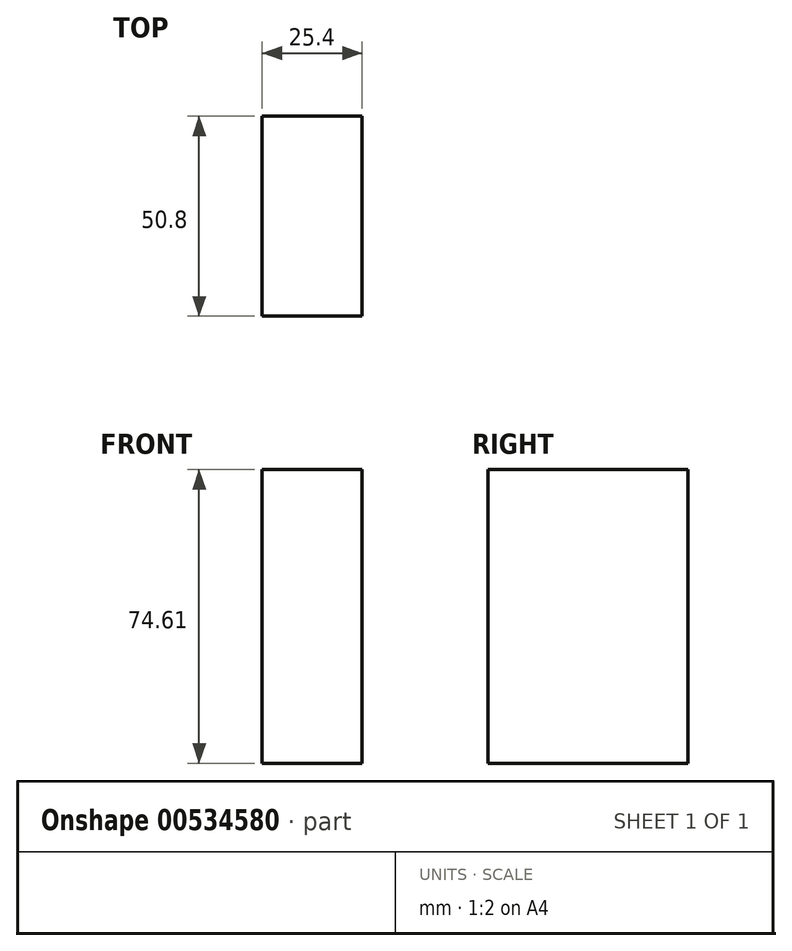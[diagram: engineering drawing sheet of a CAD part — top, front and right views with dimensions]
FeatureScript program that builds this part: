
annotation { "Feature Type Name" : "Feature", "Feature Type Description" : "" }
export const myFeature = defineFeature(function(context is Context, id is Id, definition is map)
    precondition{}
    {
        {
            var Q0;
            Q0=qCreatedBy(makeId("Right.planeOp"),FACE);
            var sketch = newSketch(context, id + "F0", { "sketchPlane" : qUnion([Q0])});
            skLineSegment(sketch, "E0.bottom", {"start": v(0, 0) * mm, "end": v(-50.8, 0) * mm});
            skLineSegment(sketch, "E0.top", {"start": v(0, 74.61) * mm, "end": v(-50.8, 74.61) * mm});
            skLineSegment(sketch, "E0.left", {"start": v(0, 0) * mm, "end": v(0, 74.61) * mm});
            skLineSegment(sketch, "E0.right", {"start": v(-50.8, 0) * mm, "end": v(-50.8, 74.61) * mm});
            skPoint(sketch, "E1.endSnap0", {"position": v(-25.4, 0) * mm});
            skSolve(sketch);
        }
        {
            var Q0;
            Q0=makeQuery(id+"F0.imprint","IMPRINT",FACE,{"disambiguationData":[TD([[makeQuery(id+"F0.imprint","IMPRINT",EDGE,{"derivedFrom":sQuery(id+"F0.wireOp",EDGE,"E0.bottom")}),-1.0]])]});
            extrude(context, id + "F1", {"entities" : qUnion([Q0]), "depth" : 25.4 * mm, "offsetDistance" : 25.4 * mm});
        }
    });
